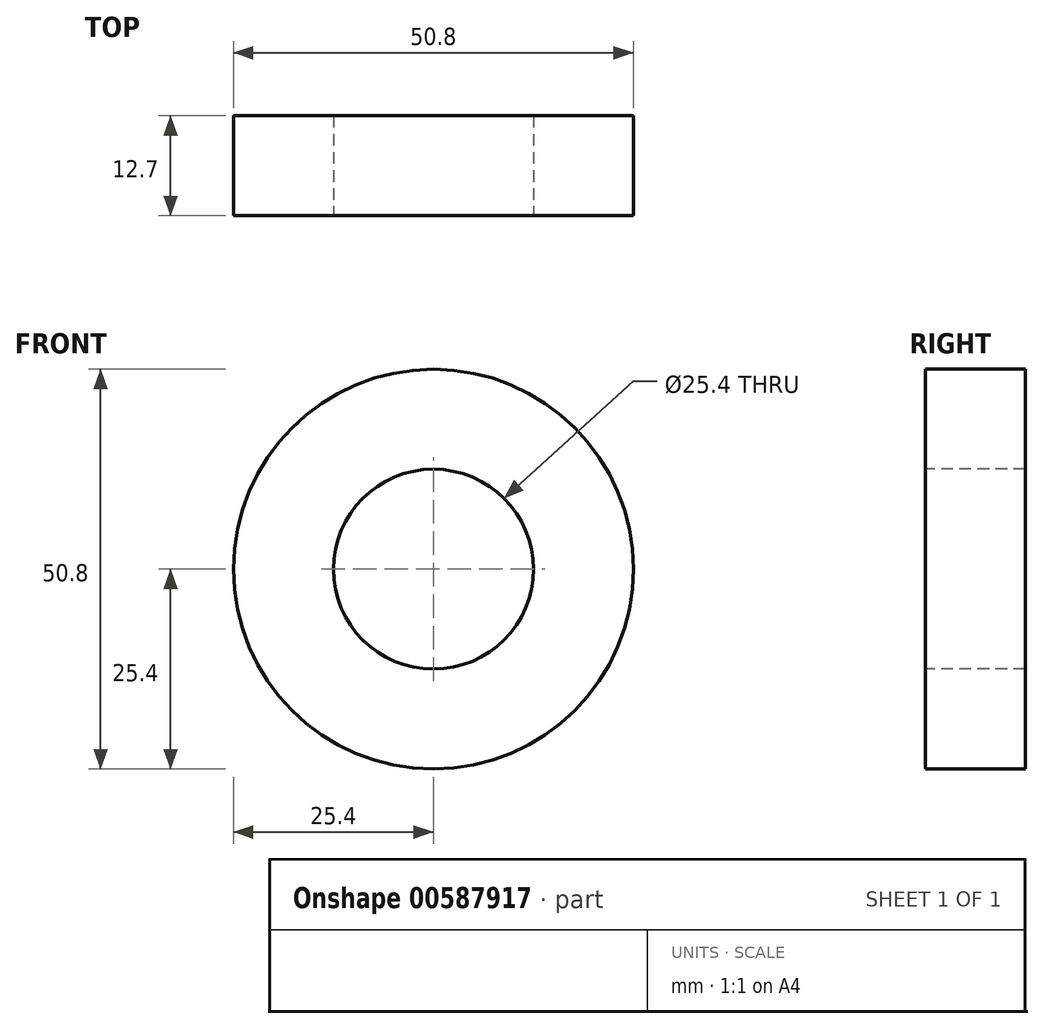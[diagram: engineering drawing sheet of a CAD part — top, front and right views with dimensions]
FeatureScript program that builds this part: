
annotation { "Feature Type Name" : "Feature", "Feature Type Description" : "" }
export const myFeature = defineFeature(function(context is Context, id is Id, definition is map)
    precondition{}
    {
        {
            var Q0;
            Q0=qCreatedBy(makeId("Front.planeOp"),FACE);
            var sketch = newSketch(context, id + "F0", { "sketchPlane" : qUnion([Q0])});
            skCircle(sketch, "E0", {"center": v(0, 0) * mm, "radius": 25.4 * mm});
            skSolve(sketch);
        }
        {
            var Q0;
            Q0 = qSketchRegion(id + "F0", true);
            extrude(context, id + "F1", {"entities" : qUnion([Q0]), "depth" : 12.7 * mm, "offsetDistance" : 25.4 * mm});
        }
        {
            var Q0;
            Q0=makeQuery(id+"F1.opExtrude","CAP_FACE",FACE,{"disambiguationData":[OSD([sQuery(id+"F0.wireOp",EDGE,"E0")])],"isStart":false});
            var sketch = newSketch(context, id + "F2", { "sketchPlane" : qUnion([Q0])});
            skCircle(sketch, "E1", {"center": v(0, 0) * mm, "radius": 12.7 * mm});
            skSolve(sketch);
        }
        {
            var Q0;
            Q0 = qSketchRegion(id + "F2", true);
            extrude(context, id + "F3", {"entities" : qUnion([Q0]), "operationType" : NewBodyOperationType.REMOVE, "oppositeDirection" : true, "depth" : 25.4 * mm, "offsetDistance" : 25.4 * mm, "hasSecondDirection" : true, "secondDirectionOppositeDirection" : false, "secondDirectionDepth" : 25.4 * mm});
        }
    });
